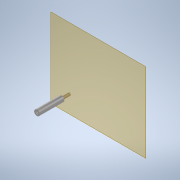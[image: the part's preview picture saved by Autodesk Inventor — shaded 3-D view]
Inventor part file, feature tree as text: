
AUTODESK INVENTOR PART (.ipt)
format: ipt  version: 2020 (Build 240168000, 168)  size: 111,616 bytes
history: native  units: in
note: dims shown in document units (in); Inventor stores cm internally (conversion verified against a paired STEP export)
features: other x6, extrude x3, sketch x3, plane x2, reference x1
ambient origin geometry x8: Origin, YZ Plane, XZ Plane, XY Plane, X Axis, Y Axis, Z Axis, Center Point
bodies: Solid1 (feature_tree)
feature tree (15):
  plane  "Work Plane1"
  extrude  "Extrusion1"  Depth=0.25in
  plane  "Work Plane2"
  extrude  "Extrusion3"  Depth=0.25in TaperAngle=0.0deg
  extrude  "Extrusion4"  [1 undecoded]
  sketch  "Sketch1"  dims[d0=0.25in d1=0.0in d5=0.1772in]
  reference  "Reference1"
  sketch  "Sketch2"  dims[d6=0.7874in d7=0.0in d8=0.25in d9=0.0in]
  sketch  "Sketch3"
  other  "<userpath>\Documents\Inventor\Drone\Assembly.iam"
  other  "Assembly.iam"
  other  "Frame:1"
  other  "DJI F330 qoadrotor arm:1"
  other  "DJI F330 qoadrotor arm v2"
  other  "holder:1"
note: 1 required parameter value undecoded (feature->parameter linkage not recoverable at this tier; creation-order binding heuristic only, values carry confidence <= 0.55)
